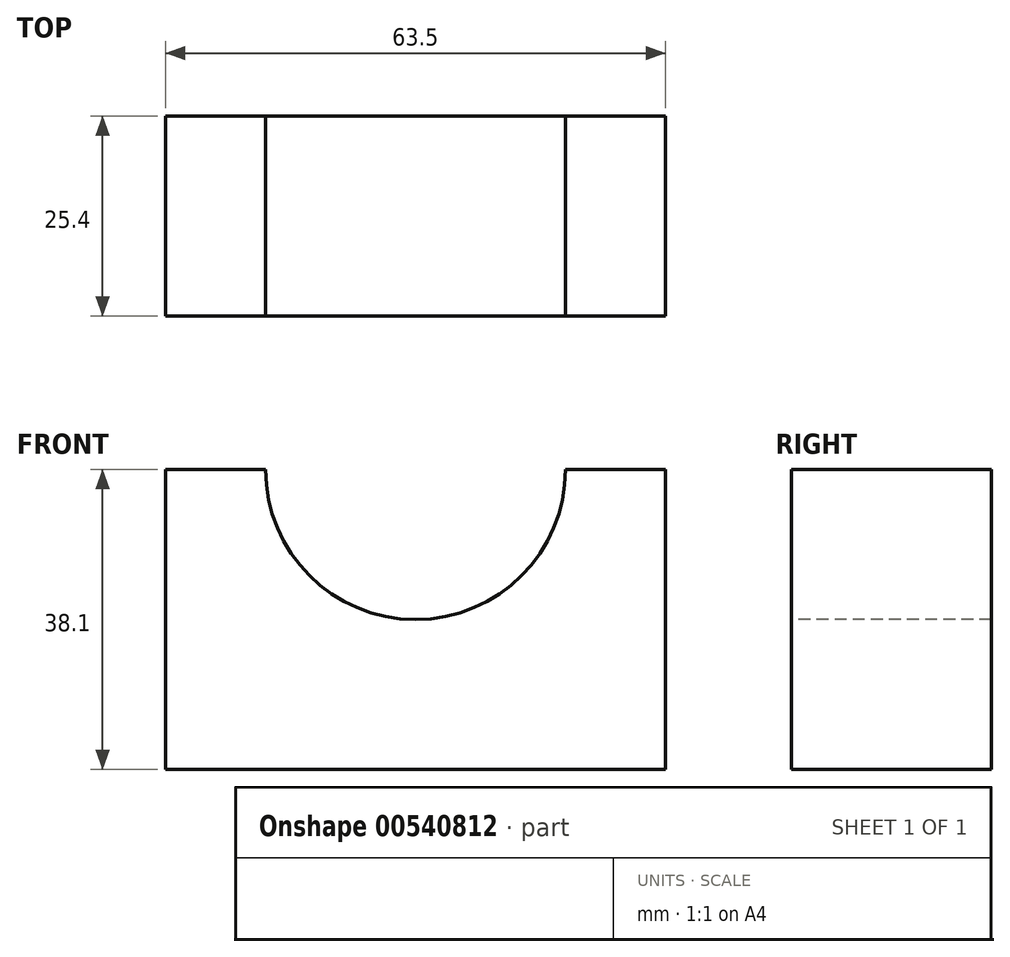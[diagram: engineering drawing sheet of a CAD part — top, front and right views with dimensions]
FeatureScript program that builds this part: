
annotation { "Feature Type Name" : "Feature", "Feature Type Description" : "" }
export const myFeature = defineFeature(function(context is Context, id is Id, definition is map)
    precondition{}
    {
        {
            var Q0;
            Q0=qCreatedBy(makeId("Front.planeOp"),FACE);
            var sketch = newSketch(context, id + "F0", { "sketchPlane" : qUnion([Q0])});
            skLineSegment(sketch, "E0", {"start": v(0, 0) * mm, "end": v(0, 38.1) * mm});
            skLineSegment(sketch, "E1", {"start": v(0, 38.1) * mm, "end": v(63.5, 38.1) * mm});
            skLineSegment(sketch, "E2", {"start": v(63.5, 38.1) * mm, "end": v(63.5, 0) * mm});
            skLineSegment(sketch, "E3", {"start": v(63.5, 0) * mm, "end": v(0, 0) * mm});
            skSolve(sketch);
        }
        {
            var Q0;
            Q0=makeQuery(id+"F0.imprint","IMPRINT",FACE,{"disambiguationData":[TD([[makeQuery(id+"F0.imprint","IMPRINT",EDGE,{"derivedFrom":sQuery(id+"F0.wireOp",EDGE,"E0")}),-1.0]])]});
            extrude(context, id + "F1", {"entities" : qUnion([Q0]), "depth" : 25.4 * mm, "offsetDistance" : 25.4 * mm});
        }
        {
            var Q0;
            Q0=makeQuery(id+"F1.opExtrude","CAP_FACE",FACE,{"disambiguationData":[OSD([sQuery(id+"F0.wireOp",EDGE,"E0"),sQuery(id+"F0.wireOp",EDGE,"E1"),sQuery(id+"F0.wireOp",EDGE,"E2"),sQuery(id+"F0.wireOp",EDGE,"E3")])],"isStart":false});
            var sketch = newSketch(context, id + "F2", { "sketchPlane" : qUnion([Q0])});
            skCircle(sketch, "E4", {"center": v(31.75, 38.1) * mm, "radius": 19.05 * mm});
            skSolve(sketch);
        }
        {
            var Q0;
            {var subQ0=sQuery(id+"F2.wireOp",EDGE,"E4");var subQ1=makeQuery(id+"F1.opExtrude","CAP_EDGE",EDGE,{"disambiguationData":[OSD([sQuery(id+"F0.wireOp",EDGE,"E1")])],"isStart":false});var subQ2=makeQuery(id+"F2.imprint","INTERSECT",VERTEX,{"disambiguationData":[OD(0.0)],"derivedFrom":[subQ1,subQ0]});Q0=makeQuery(id+"F2.imprint","IMPRINT",FACE,{"disambiguationData":[TD([[makeQuery(id+"F2.imprint","IMPRINT",EDGE,{"disambiguationData":[TD([[subQ2,1.0]])],"derivedFrom":subQ0}),1.0]])]});}
            var Q1;
            {var subQ0=sQuery(id+"F2.wireOp",EDGE,"E4");var subQ1=makeQuery(id+"F1.opExtrude","CAP_EDGE",EDGE,{"disambiguationData":[OSD([sQuery(id+"F0.wireOp",EDGE,"E1")])],"isStart":false});var subQ2=makeQuery(id+"F2.imprint","INTERSECT",VERTEX,{"disambiguationData":[OD(0.0)],"derivedFrom":[subQ1,subQ0]});Q1=makeQuery(id+"F2.imprint","IMPRINT",FACE,{"disambiguationData":[TD([[makeQuery(id+"F2.imprint","IMPRINT",EDGE,{"disambiguationData":[TD([[subQ2,-1.0]])],"derivedFrom":subQ0}),1.0]])]});}
            extrude(context, id + "F3", {"entities" : qUnion([Q0, Q1]), "operationType" : NewBodyOperationType.REMOVE, "oppositeDirection" : true, "depth" : 25.4 * mm, "offsetDistance" : 25.4 * mm});
        }
    });
